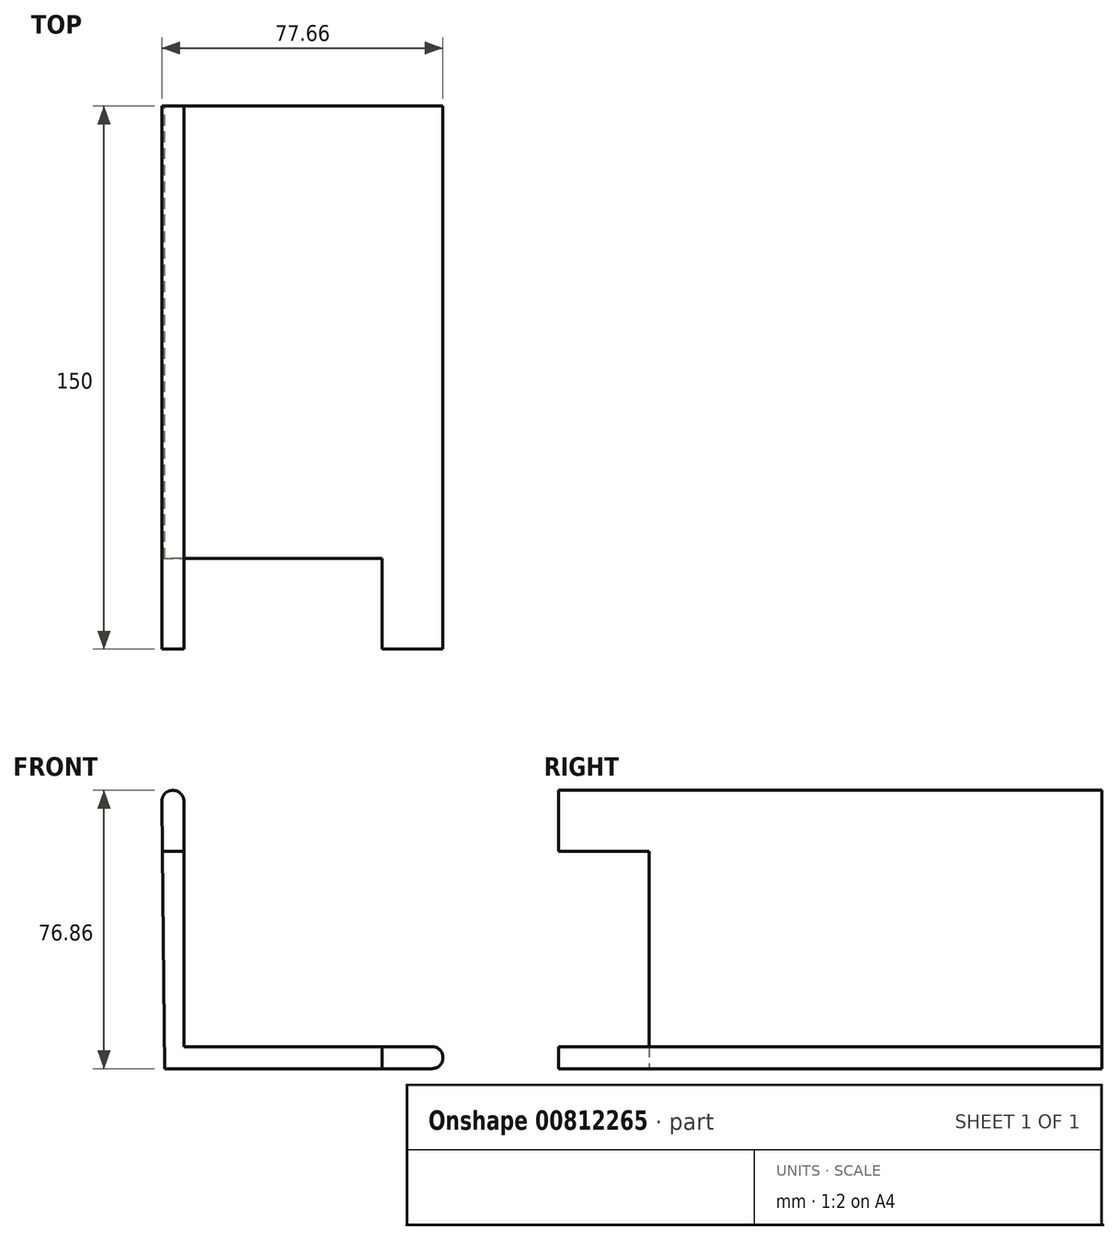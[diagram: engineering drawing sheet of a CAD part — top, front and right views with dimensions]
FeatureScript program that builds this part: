
annotation { "Feature Type Name" : "Feature", "Feature Type Description" : "" }
export const myFeature = defineFeature(function(context is Context, id is Id, definition is map)
    precondition{}
    {
        {
            var Q0;
            Q0=qCreatedBy(makeId("Front.planeOp"),FACE);
            var sketch = newSketch(context, id + "F0", { "sketchPlane" : qUnion([Q0])});
            skLineSegment(sketch, "E0", {"start": v(-38.63, 32.12) * mm, "end": v(-32.53, 32.12) * mm});
            skLineSegment(sketch, "E1", {"start": v(-32.53, 32.12) * mm, "end": v(-32.53, -38.64) * mm});
            skLineSegment(sketch, "E2", {"start": v(-32.53, -38.64) * mm, "end": v(39.07, -38.64) * mm});
            skLineSegment(sketch, "E3", {"start": v(39.07, -38.64) * mm, "end": v(39.07, -44.74) * mm});
            skLineSegment(sketch, "E4", {"start": v(39.07, -44.74) * mm, "end": v(-37.8, -44.74) * mm});
            skLineSegment(sketch, "E5", {"start": v(-37.8, -44.74) * mm, "end": v(-38.63, 32.12) * mm});
            skLineSegment(sketch, "E6", {"start": v(-38.44, 15.26) * mm, "end": v(-32.53, 15.33) * mm});
            skLineSegment(sketch, "E7", {"start": v(22.2, -38.64) * mm, "end": v(22.2, -44.74) * mm});
            skSolve(sketch);
        }
        {
            var Q0;
            Q0=makeQuery(id+"F0.imprint","IMPRINT",FACE,{"disambiguationData":[TD([[makeQuery(id+"F0.imprint","IMPRINT",EDGE,{"derivedFrom":sQuery(id+"F0.wireOp",EDGE,"E0")}),-1.0]])]});
            var Q1;
            {var subQ3=sQuery(id+"F0.wireOp",EDGE,"E6");Q1=makeQuery(id+"F0.imprint","IMPRINT",FACE,{"disambiguationData":[TD([[makeQuery(id+"F0.imprint","IMPRINT",EDGE,{"derivedFrom":subQ3}),-1.0]])]});}
            var Q2;
            {var subQ0=sQuery(id+"F0.wireOp",EDGE,"E3");Q2=makeQuery(id+"F0.imprint","IMPRINT",FACE,{"disambiguationData":[TD([[makeQuery(id+"F0.imprint","IMPRINT",EDGE,{"derivedFrom":subQ0}),-1.0]])]});}
            extrude(context, id + "F1", {"entities" : qUnion([Q0, Q1, Q2]), "flatOperationType" : FlatOperationType.REMOVE, "depth" : 74.9 * mm, "offsetDistance" : 25 * mm, "domain" : OperationDomain.MODEL});
        }
        {
            var Q0;
            Q0=makeQuery(id+"F1.opExtrude","CAP_FACE",FACE,{"disambiguationData":[OSD([sQuery(id+"F0.wireOp",EDGE,"E0"),sQuery(id+"F0.wireOp",EDGE,"E1"),sQuery(id+"F0.wireOp",EDGE,"E2"),sQuery(id+"F0.wireOp",EDGE,"E3"),sQuery(id+"F0.wireOp",EDGE,"E4"),sQuery(id+"F0.wireOp",EDGE,"E5")])],"isStart":true});
            extrude(context, id + "F2", {"entities" : qUnion([Q0]), "operationType" : NewBodyOperationType.ADD, "flatOperationType" : FlatOperationType.REMOVE, "depth" : 75.1 * mm, "offsetDistance" : 25 * mm, "domain" : OperationDomain.MODEL});
        }
        {
            var Q0;
            {var subQ0=sQuery(id+"F0.wireOp",EDGE,"E1");var subQ1=sQuery(id+"F0.wireOp",EDGE,"E0");Q0=makeQuery(id+"F2.boolean.opBoolean","MERGE",EDGE,{"derivedFrom":[makeQuery(id+"F1.opExtrude","SWEPT_EDGE",EDGE,{"disambiguationData":[OSD([subQ1,subQ0])]}),makeQuery(id+"F2.opExtrude","SWEPT_EDGE",EDGE,{"disambiguationData":[OSD([subQ1,subQ0])]})]});}
            var Q1;
            {var subQ0=sQuery(id+"F0.wireOp",EDGE,"E5");var subQ1=sQuery(id+"F0.wireOp",EDGE,"E0");Q1=makeQuery(id+"F2.boolean.opBoolean","MERGE",EDGE,{"derivedFrom":[makeQuery(id+"F1.opExtrude","SWEPT_EDGE",EDGE,{"disambiguationData":[OSD([subQ1,subQ0])]}),makeQuery(id+"F2.opExtrude","SWEPT_EDGE",EDGE,{"disambiguationData":[OSD([subQ1,subQ0])]})]});}
            var Q2;
            {var subQ0=sQuery(id+"F0.wireOp",EDGE,"E4");var subQ1=sQuery(id+"F0.wireOp",EDGE,"E3");Q2=makeQuery(id+"F2.boolean.opBoolean","MERGE",EDGE,{"derivedFrom":[makeQuery(id+"F1.opExtrude","SWEPT_EDGE",EDGE,{"disambiguationData":[OSD([subQ1,subQ0])]}),makeQuery(id+"F2.opExtrude","SWEPT_EDGE",EDGE,{"disambiguationData":[OSD([subQ1,subQ0])]})]});}
            var Q3;
            {var subQ0=sQuery(id+"F0.wireOp",EDGE,"E3");var subQ1=sQuery(id+"F0.wireOp",EDGE,"E2");Q3=makeQuery(id+"F2.boolean.opBoolean","MERGE",EDGE,{"derivedFrom":[makeQuery(id+"F1.opExtrude","SWEPT_EDGE",EDGE,{"disambiguationData":[OSD([subQ1,subQ0])]}),makeQuery(id+"F2.opExtrude","SWEPT_EDGE",EDGE,{"disambiguationData":[OSD([subQ1,subQ0])]})]});}
            fillet(context, id + "F3", {"entities" : qUnion([Q0, Q1, Q2, Q3]), "radius" : 3 * mm, "tangentPropagation" : true, "defaultsChanged" : false, "vertexSettings" : [], "allowEdgeOverflow" : false});
        }
        {
            var Q0;
            Q0=makeQuery(id+"F1.opExtrude","CAP_FACE",FACE,{"disambiguationData":[OSD([sQuery(id+"F0.wireOp",EDGE,"E0"),sQuery(id+"F0.wireOp",EDGE,"E1"),sQuery(id+"F0.wireOp",EDGE,"E2"),sQuery(id+"F0.wireOp",EDGE,"E3"),sQuery(id+"F0.wireOp",EDGE,"E4"),sQuery(id+"F0.wireOp",EDGE,"E5")])],"isStart":false});
            var sketch = newSketch(context, id + "F4", { "sketchPlane" : qUnion([Q0])});
            skLineSegment(sketch, "E8", {"start": v(-38.44, 15.26) * mm, "end": v(-32.53, 15.26) * mm});
            skLineSegment(sketch, "E9", {"start": v(-32.53, 15.26) * mm, "end": v(-32.53, -35.78) * mm});
            skLineSegment(sketch, "E10", {"start": v(-32.53, -35.78) * mm, "end": v(22.2, -35.78) * mm});
            skLineSegment(sketch, "E11", {"start": v(22.2, -35.78) * mm, "end": v(22.2, -44.74) * mm});
            skLineSegment(sketch, "E12", {"start": v(22.2, -44.74) * mm, "end": v(-37.8, -44.74) * mm});
            skLineSegment(sketch, "E13", {"start": v(-37.8, -44.74) * mm, "end": v(-38.44, 15.26) * mm});
            skSolve(sketch);
        }
        {
            var Q0;
            Q0=makeQuery(id+"F4.imprint","IMPRINT",FACE,{"disambiguationData":[TD([[makeQuery(id+"F4.imprint","IMPRINT",EDGE,{"derivedFrom":sQuery(id+"F4.wireOp",EDGE,"E8")}),-1.0]])]});
            extrude(context, id + "F5", {"entities" : qUnion([Q0]), "operationType" : NewBodyOperationType.REMOVE, "oppositeDirection" : true, "depth" : 25 * mm, "offsetDistance" : 25 * mm});
        }
    });
